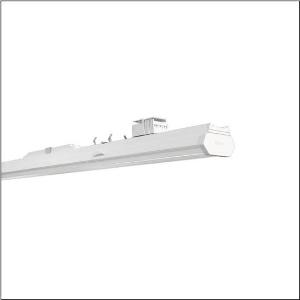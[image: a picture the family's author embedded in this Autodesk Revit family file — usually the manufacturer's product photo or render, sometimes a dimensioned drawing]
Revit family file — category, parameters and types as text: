
# Revit family: licross_r__21_protected_ho_52td11cn4c5s_1fd3
name_source: partatom
category: Lighting Fixtures
units: mm (PartAtom-declared; Revit-internal decimal feet)

## family parameters
Cut with Voids When Loaded = No
Host = Face
Light Source = No
Part Type = Normal
Room Calculation Point = No
Round Connector Dimension = Use Diameter
Shared = No

## types (1)
- --- (1 x LED, 12650 lm, 68.9 W, 4000K)
    Apparent Load = 69 VA
    CIE Flux Codes = 84 94 98 99 100
    Color Rendering = 80
    Color Temperature = 4000K
    Default Elevation = 1800 mm
    Description = Licross® 21 Protected HO, luminaire insert, of sheet steel, galvanised, coil coated, white, length: 1.500mm, width: 66mm, height: 67mm, LED rated luminous flux: 12.650lm, light colour: 840, control gear: ON/OFF Multilumen, CLOi, control gear: ECG Multilumen, with plug, 3-pole, with phase selection, mains connection: 220..240V, AC, 50/60Hz, start of lifetime: 69W, end of service life: 83W, halogen-free wiring, primary light control with lens, of plastic, primary optical cover: cover, of PMMA, light emission: direct distribution, primary light characteristic: symmetric, protection rating (complete): IP54, insulation class (complete): insulation class I (protective earthing), certification: CE, ENEC, VDE, UKCA, protection symbol: D if used in an environment with non-conductive dust loads with corresponding accessories, impact resistance: IK06, permissible ambient temperature for indoor applications: -35..+35°C, corresponds to IFS (International Featured Standards) requirements for safety and quality in the food industry, reducing of maximum allowable ambient temperature of 5°C with ceiling mounting, LABS conformity tested according to VDMA 24364:2018-05, packaging unit: 1 piece
    Height = 92 mm
    Lamp = 1 x LED
    Lamp Light Flux = 12650 lm
    Lamp Power = 68.9 W
    Lamp count = 1
    Length = 1500 mm
    Luminous efficacy = 184 lm/W
    Manufacturer = Siteco
    ModVariant = No
    Model = 52TD11CN4C5S
    Mounting Place = Ceiling
    Mounting Type = Pendant
    Number of Poles = 1
    OnlyDefault = Yes
    Power Factor = 1
    Product Name = Licross® 21 Protected HO
    Product group = luminaire insert
    ProductGroupID = 901
    Protection Class = Protection class I
    Protection Degree = IP 54
    RLX_Detail_Level = 1
    RLX_Emergency_Light_Flux = 0 lm
    RLX_Emergency_Type = 0
    RLX_Emergency_Type_DB = No
    RlxData = <blob elided: 22085 chars, md5=5443e8b1>
    Socket = socket
    Standby Power = 0 W
    System Light Flux = 12650 lm
    System Power = 69 W
    Type Comments = factory setting: luminous flux: 100 % | (A | C | E) | 162 mA
    Type Image = l_1256148.jpg
    URL = http://relux.com
    VarID = @adj_059151
    Voltage = 0 V
    Weight = 0.00 kg
    Width = 88 mm

## geometry (parser evidence)
native form markers: Blend x4, Sweep x12
no freeform markers — native parametric forms only
